# Revit family: 1 SOUND_Cannon C8 Clamp Mounted
name_source: partatom
category: Communication Devices
units: mm (PartAtom-declared; Revit-internal decimal feet)

## family parameters
Cut with Voids When Loaded = No
Host = Face
Maintain Annotation Orientation = No
Part Type = Normal
Room Calculation Point = No
Round Connector Dimension = Use Diameter
Shared = No

## types (2) — shared parameters
Bandwidth = 55 Hz - 18 kHz (-6 dB)
Category = Speaker
Construction = Finland birch plywood (urea glue), polyurea, clear matte salt and UV resistant coating, 316 stainless steel hardware, 3D spacer mesh fabric
Default Elevation = 2438.40 mm
Depth - Overall = 220.55 mm
Dimensions (HxWxD) = 10.2” (260 mm) x 10.2” (260 mm) x 10.2” (260 mm)
Impedance = 8Ω
Manufacturer = 1 SOUND
Model = C8
Power = 400 watts (program), 200 watts (AES)
Rigging = (4) M6 points
URL = https://www.1-sound.com
Weight = 18.4 lb / 8.3 kg
Width - Mounting Holes = 110.00 mm
Width - Overall = 268.00 mm

## per-type parameters (varying)
| type | Accessory Used | Connectors | Speaker Type |
| C8 With Clamp | C-Clamp; C8 | (2) NL4, 2-circuit switch, (1) Neutrik NDL dummyPlug | 1 SOUND_Cannon_C8 : C8 |
| C8i With Clamp | C-Clamp; C8i | (1) screw terminal block with input +/- and loop +/- | 1 SOUND_Cannon_C8 : C8i |

## geometry (parser evidence)
native form markers: Sweep x14
no freeform markers — native parametric forms only
